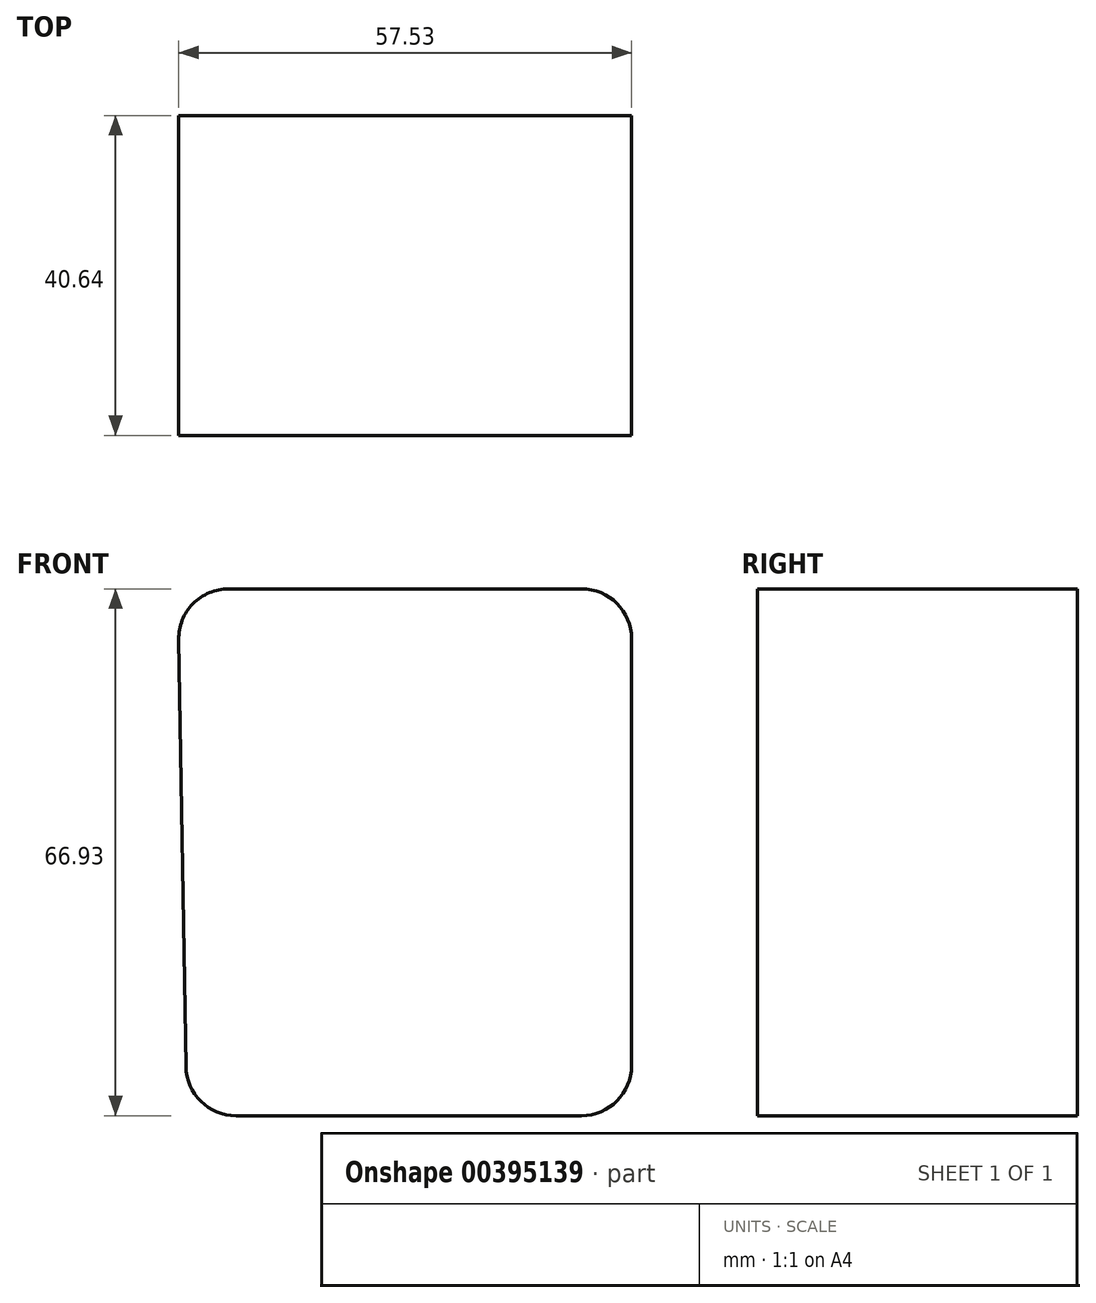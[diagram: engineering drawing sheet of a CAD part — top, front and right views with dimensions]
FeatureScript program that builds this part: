
annotation { "Feature Type Name" : "Feature", "Feature Type Description" : "" }
export const myFeature = defineFeature(function(context is Context, id is Id, definition is map)
    precondition{}
    {
        {
            var Q0;
            Q0=qCreatedBy(makeId("Front.planeOp"),FACE);
            var sketch = newSketch(context, id + "F0", { "sketchPlane" : qUnion([Q0])});
            skLineSegment(sketch, "E0", {"start": v(-19.23, 32.23) * mm, "end": v(25.6, 32.23) * mm});
            skLineSegment(sketch, "E1", {"start": v(31.95, 25.88) * mm, "end": v(31.95, -28.35) * mm});
            skLineSegment(sketch, "E2", {"start": v(25.6, -34.7) * mm, "end": v(-18.3, -34.7) * mm});
            skLineSegment(sketch, "E3", {"start": v(-24.66, -28.45) * mm, "end": v(-25.58, 25.77) * mm});
            skPoint(sketch, "E4.visualSharp", {"position": v(-24.55, -34.7) * mm});
            skArc(sketch, "E4.filletArc", {"start": v(-24.66, -28.45) * mm, "mid": v(-22.76, -32.87) * mm, "end": v(-18.3, -34.7) * mm});
            skPoint(sketch, "E5.visualSharp", {"position": v(31.95, -34.7) * mm});
            skArc(sketch, "E5.filletArc", {"start": v(25.6, -34.7) * mm, "mid": v(30.09, -32.84) * mm, "end": v(31.95, -28.35) * mm});
            skPoint(sketch, "E6.visualSharp", {"position": v(31.95, 32.23) * mm});
            skArc(sketch, "E6.filletArc", {"start": v(31.95, 25.88) * mm, "mid": v(30.09, 30.37) * mm, "end": v(25.6, 32.23) * mm});
            skPoint(sketch, "E7.visualSharp", {"position": v(-25.7, 32.23) * mm});
            skArc(sketch, "E7.filletArc", {"start": v(-19.23, 32.23) * mm, "mid": v(-23.76, 30.33) * mm, "end": v(-25.58, 25.77) * mm});
            skSolve(sketch);
        }
        {
            var Q0;
            Q0=makeQuery(id+"F0.imprint","IMPRINT",FACE,{"disambiguationData":[TD([[makeQuery(id+"F0.imprint","IMPRINT",EDGE,{"derivedFrom":sQuery(id+"F0.wireOp",EDGE,"E0")}),-1.0]])]});
            var Q1;
            Q1 = qSketchRegion(id + "F0", true);
            extrude(context, id + "F1", {"entities" : qUnion([Q0, Q1]), "depth" : 40.64 * mm});
        }
    });
